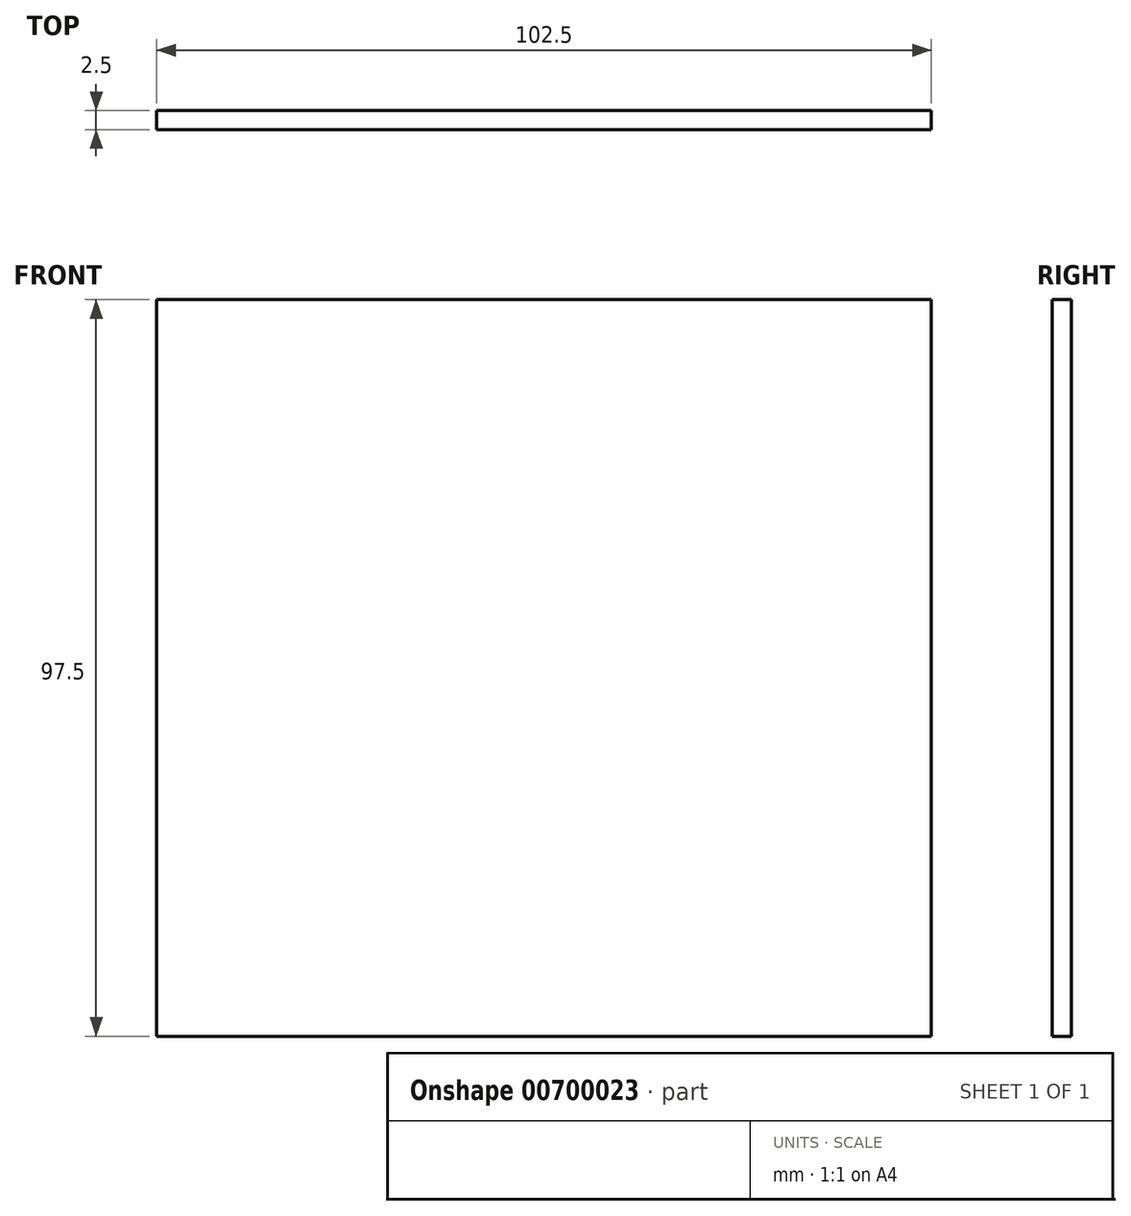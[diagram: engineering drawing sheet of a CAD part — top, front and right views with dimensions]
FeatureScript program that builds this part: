
annotation { "Feature Type Name" : "Feature", "Feature Type Description" : "" }
export const myFeature = defineFeature(function(context is Context, id is Id, definition is map)
    precondition{}
    {
        {
            var Q0;
            Q0=qCreatedBy(makeId("Front.planeOp"),FACE);
            var sketch = newSketch(context, id + "F0", { "sketchPlane" : qUnion([Q0])});
            skLineSegment(sketch, "E0.bottom", {"start": v(51.25, -48.75) * mm, "end": v(-51.25, -48.75) * mm});
            skLineSegment(sketch, "E0.top", {"start": v(51.25, 48.75) * mm, "end": v(-51.25, 48.75) * mm});
            skLineSegment(sketch, "E0.left", {"start": v(51.25, -48.75) * mm, "end": v(51.25, 48.75) * mm});
            skLineSegment(sketch, "E0.right", {"start": v(-51.25, -48.75) * mm, "end": v(-51.25, 48.75) * mm});
            skPoint(sketch, "E0.middle", {"position": v(0, 0) * mm});
            skSolve(sketch);
        }
        {
            var Q0;
            Q0 = qSketchRegion(id + "F0", true);
            extrude(context, id + "F1", {"entities" : qUnion([Q0]), "depth" : 2.5 * mm, "offsetDistance" : 25 * mm});
        }
    });
